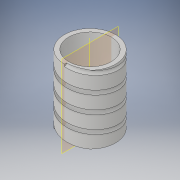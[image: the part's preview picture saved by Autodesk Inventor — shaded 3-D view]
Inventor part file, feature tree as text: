
AUTODESK INVENTOR PART (.ipt)
format: ipt  version: 2019.2 (Build 232265000, 265)  size: 218,624 bytes
history: native  units: in
note: dims shown in document units (in); Inventor stores cm internally (conversion verified against a paired STEP export)
features: sketch x2, extrude x1, helix x1
ambient origin geometry x8: Origin, YZ Plane, XZ Plane, XY Plane, X Axis, Y Axis, Z Axis, Center Point
bodies: Solid1 (feature_tree)
feature tree (4):
  extrude  "Extrusion1"  Depth=1.25in
  helix  "Coil1"  [1 undecoded]
  sketch  "Sketch1"  dims[d0=2.0in d1=0.0in d4=1.25in d5=1.5in]
  sketch  "Sketch2"  dims[d10=0.5in d11=1.0in d12=1.9685in d13=0.0in d14=90.0deg d15=90.0deg d16=0.0in d17=0.0in d18=0.125in]
note: 1 required parameter value undecoded (feature->parameter linkage not recoverable at this tier; creation-order binding heuristic only, values carry confidence <= 0.55)
